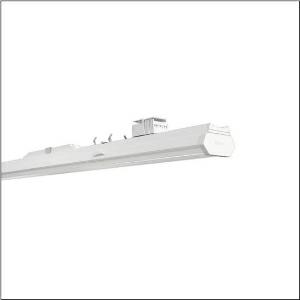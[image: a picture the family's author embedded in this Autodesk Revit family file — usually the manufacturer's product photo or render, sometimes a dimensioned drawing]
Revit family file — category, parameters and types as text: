
# Revit family: licross_r__11_protected_ho_51td11cn4exs_ee6c
name_source: partatom
category: Lighting Fixtures
units: mm (PartAtom-declared; Revit-internal decimal feet)

## family parameters
Cut with Voids When Loaded = No
Host = Face
Light Source = No
Part Type = Normal
Room Calculation Point = No
Round Connector Dimension = Use Diameter
Shared = No

## types (1)
- --- (1 x LED, 14460 lm, 77.6 W, 4000K)
    Apparent Load = 78 VA
    CIE Flux Codes = 84 94 98 99 100
    Color Rendering = 80
    Color Temperature = 4000K
    Default Elevation = 1800 mm
    Description = Licross® 11 Protected HO, luminaire insert, of sheet steel, galvanised, coil coated, white, length: 1.500mm, width: 90mm, height: 101mm, LED rated luminous flux: 14.460lm, light colour: 840, control gear: ON/OFF Multilumen, CLOi, with plug, 3-pole, with phase selection, mains connection: 220..240V, AC, 50/60Hz, start of lifetime: 78W, end of service life: 87W, halogen-free wiring, primary light control with lens, of plastic, primary optical cover: cover, of PMMA, light emission: direct distribution, primary light characteristic: symmetric, protection rating (complete): IP54, insulation class (complete): insulation class I (protective earthing), certification: CE, ENEC, VDE, UKCA, protection symbol: D if used in an environment with non-conductive dust loads with corresponding accessories, impact resistance: IK06, permissible ambient temperature for indoor applications: -35..+35°C, corresponds to IFS (International Featured Standards) requirements for safety and quality in the food industry, reducing of maximum allowable ambient temperature of 5°C with ceiling mounting, LABS conformity tested according to VDMA 24364:2018-05, packaging unit: 1 piece
    Height = 92 mm
    Lamp = 1 x LED
    Lamp Light Flux = 14460 lm
    Lamp Power = 77.6 W
    Lamp count = 1
    Length = 1500 mm
    Luminous efficacy = 186 lm/W
    Manufacturer = Siteco
    ModVariant = No
    Model = 51TD11CN4EXS
    Mounting Place = Ceiling
    Mounting Type = Pendant
    Number of Poles = 1
    OnlyDefault = Yes
    Power Factor = 1
    Product Name = Licross® 11 Protected HO
    Product group = luminaire insert
    ProductGroupID = 902
    Protection Class = Protection class I
    Protection Degree = IP 54
    RLX_Detail_Level = 1
    RLX_Emergency_Light_Flux = 0 lm
    RLX_Emergency_Type = 0
    RLX_Emergency_Type_DB = No
    RlxData = <blob elided: 22201 chars, md5=34c8f90a>
    Socket = socket
    Standby Power = 0 W
    System Light Flux = 14460 lm
    System Power = 78 W
    Type Comments = factory setting: luminous flux: 100 % | (A | C | E) | 181 mA
    Type Image = l_1256145.jpg
    URL = http://relux.com
    VarID = @adj_085824
    Voltage = 0 V
    Weight = 0.00 kg
    Width = 88 mm

## geometry (parser evidence)
native form markers: Blend x4, Sweep x11
no freeform markers — native parametric forms only
